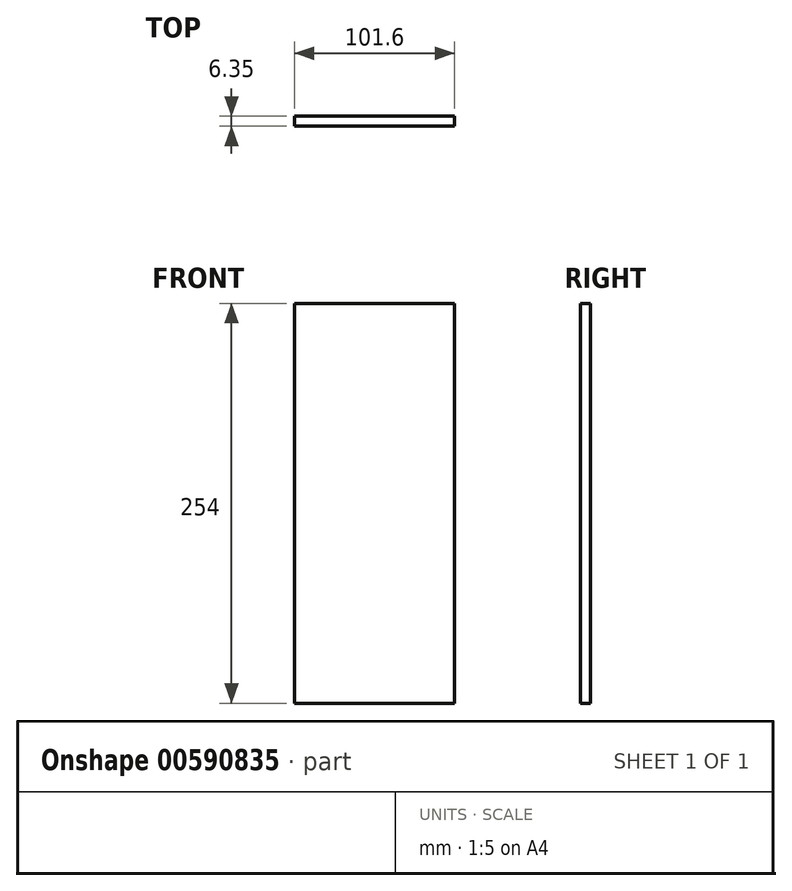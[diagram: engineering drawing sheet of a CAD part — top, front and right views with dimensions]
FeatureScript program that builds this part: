
annotation { "Feature Type Name" : "Feature", "Feature Type Description" : "" }
export const myFeature = defineFeature(function(context is Context, id is Id, definition is map)
    precondition{}
    {
        {
            var Q0;
            Q0=qCreatedBy(makeId("Front.planeOp"),FACE);
            var sketch = newSketch(context, id + "F0", { "sketchPlane" : qUnion([Q0])});
            skLineSegment(sketch, "E0", {"start": v(-50.08, 229.59) * mm, "end": v(51.52, 229.59) * mm});
            skLineSegment(sketch, "E1", {"start": v(51.52, 229.59) * mm, "end": v(51.52, -24.41) * mm});
            skLineSegment(sketch, "E2", {"start": v(51.52, -24.41) * mm, "end": v(-50.08, -24.41) * mm});
            skLineSegment(sketch, "E3", {"start": v(-50.08, -24.41) * mm, "end": v(-50.08, 229.59) * mm});
            skPoint(sketch, "E4.orphan", {"position": v(-50.08, 46) * mm});
            skSolve(sketch);
        }
        {
            var Q0;
            Q0=makeQuery(id+"F0.imprint","IMPRINT",FACE,{"disambiguationData":[TD([[makeQuery(id+"F0.imprint","IMPRINT",EDGE,{"derivedFrom":sQuery(id+"F0.wireOp",EDGE,"E0")}),-1.0]])]});
            extrude(context, id + "F1", {"entities" : qUnion([Q0]), "depth" : 6.35 * mm, "offsetDistance" : 25.4 * mm});
        }
    });
